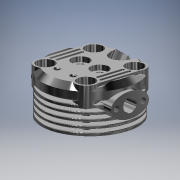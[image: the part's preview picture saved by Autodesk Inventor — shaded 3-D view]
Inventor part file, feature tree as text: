
AUTODESK INVENTOR PART (.ipt)
format: ipt  version: 2018 (Build 220112000, 112)  size: 973,824 bytes
history: native  units: mm
features: sketch x9, extrude x8, revolve x3, fillet x3, thread x3, hole x1, chamfer x1, plane x1, mirror x1
ambient origin geometry x8: Origin, YZ Plane, XZ Plane, XY Plane, X Axis, Y Axis, Z Axis, Center Point
bodies: Solid1 (feature_tree)
feature tree (30):
  revolve  "Revolution1"  [1 undecoded]
  revolve  "Revolution2"  [1 undecoded]
  extrude  "Extrusion1"  Depth=1.5mm
  sketch  "Sketch4"  dims[d6=1.5mm d7=18.0mm]
  extrude  "Extrusion2"  Depth=18.0mm
  extrude  "Extrusion3"  Depth=1.5mm
  extrude  "Extrusion4"  Depth=15.5mm
  hole  "Hole1"  [1 undecoded]
  fillet  "Fillet1"  Radius=6.0mm
  chamfer  "Chamfer1"  Angle=90.0deg  [1 undecoded]
  revolve  "Revolution3"  [1 undecoded]
  thread  "Thread1"  [1 undecoded]
  plane  "Work Plane1"
  sketch  "Sketch7"  dims[d13=2.5mm d15=11.5mm d16=6.0mm]
  extrude  "Extrusion5"  Depth=0.5mm
  extrude  "Extrusion6"  Depth=10.0mm
  extrude  "Extrusion7"  Depth=10.0mm TaperAngle=0.0deg
  thread  "Thread2"  [1 undecoded]
  thread  "Thread3"  [1 undecoded]
  extrude  "Extrusion8"  Depth=0.5mm
  mirror  "Mirror1"
  fillet  "Fillet2"  Radius=9.0mm
  fillet  "Fillet3"  Radius=4.0mm
  sketch  "Sketch1"  dims[d0=22.0mm d1=23.0mm]
  sketch  "Sketch2"  dims[d2=2.8mm d3=2.8mm]
  sketch  "Sketch3"  dims[d4=1.5mm d5=1.5mm]
  sketch  "Sketch5"  dims[d8=14.5mm d9=1.5mm]
  sketch  "Sketch6"  dims[d10=90.0deg d11=15.5mm]
  sketch  "Sketch8"  dims[d17=3.0mm]
  sketch  "Sketch9"  dims[d18=4.5mm d19=90.0deg d20=1.5mm d21=1.5mm d22=11.95mm d23=30.0mm d25=3.0mm d26=10.0mm d28=10.0mm d30=10.0mm d31=0.0mm d32=36.0mm d33=45.0deg d34=11.0mm d35=9.0mm d36=4.0mm d37=20.0mm d39=90.0deg d41=10.0mm d42=0.0mm d43=4.0mm d44=0.0mm d45=10.0mm d46=0.0mm d47=13.1mm d48=5.0mm d49=2.459mm d50=6.0mm d51=4.0mm d52=2.0mm d53=90.0deg d54=8.8mm d55=20.594885mm d56=0.5mm d57=0.5mm d58=2.0mm d59=45.0deg d60=18.0mm d61=5.585054mm d62=6.0mm d63=5.088289mm d64=3.5mm d65=12.575mm d66=90.0deg d67=10.0mm d68=0.0mm d69=7.0mm d73=10.0mm d74=6.0mm d75=12.0mm d76=10.0mm d77=2.0mm d78=0.0mm d79=0.0mm d80=10.0mm d81=0.0mm d82=3.0mm d83=7.0mm d84=10.0mm d85=0.0mm d86=10.0mm d87=0.0mm d88=10.0mm d89=0.0mm d90=9.5mm d91=6.0mm d92=12.0mm d93=6.0mm d95=3.0mm d96=0.0mm d97=0.25mm d98=0.5mm]
note: 8 required parameter values undecoded (feature->parameter linkage not recoverable at this tier; creation-order binding heuristic only, values carry confidence <= 0.55)